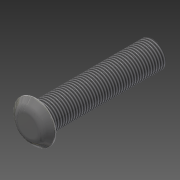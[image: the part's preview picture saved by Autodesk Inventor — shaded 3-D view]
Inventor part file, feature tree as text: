
AUTODESK INVENTOR PART (.ipt)
format: ipt  version: 2015 (Build 190159000, 159)  size: 142,848 bytes
history: native  units: mm
features: sketch x3, other x2, extrude x1, thread x1, hole x1
ambient origin geometry x8: Origin, YZ Plane, XZ Plane, XY Plane, X Axis, Y Axis, Z Axis, Center Point
bodies: Body1 (feature_tree)
feature tree (8):
  other  "Bryła1"
  extrude  "Wyciągnięcie proste1"  Depth=8.0mm
  other  "Podstawa"
  thread  "Gwint1"
  hole  "Otwór1"  [1 undecoded]
  sketch  "Szkic1"
  sketch  "Szkic3"
  sketch  "Szkic4"
note: 1 required parameter value undecoded (feature->parameter linkage not recoverable at this tier; creation-order binding heuristic only, values carry confidence <= 0.55)
